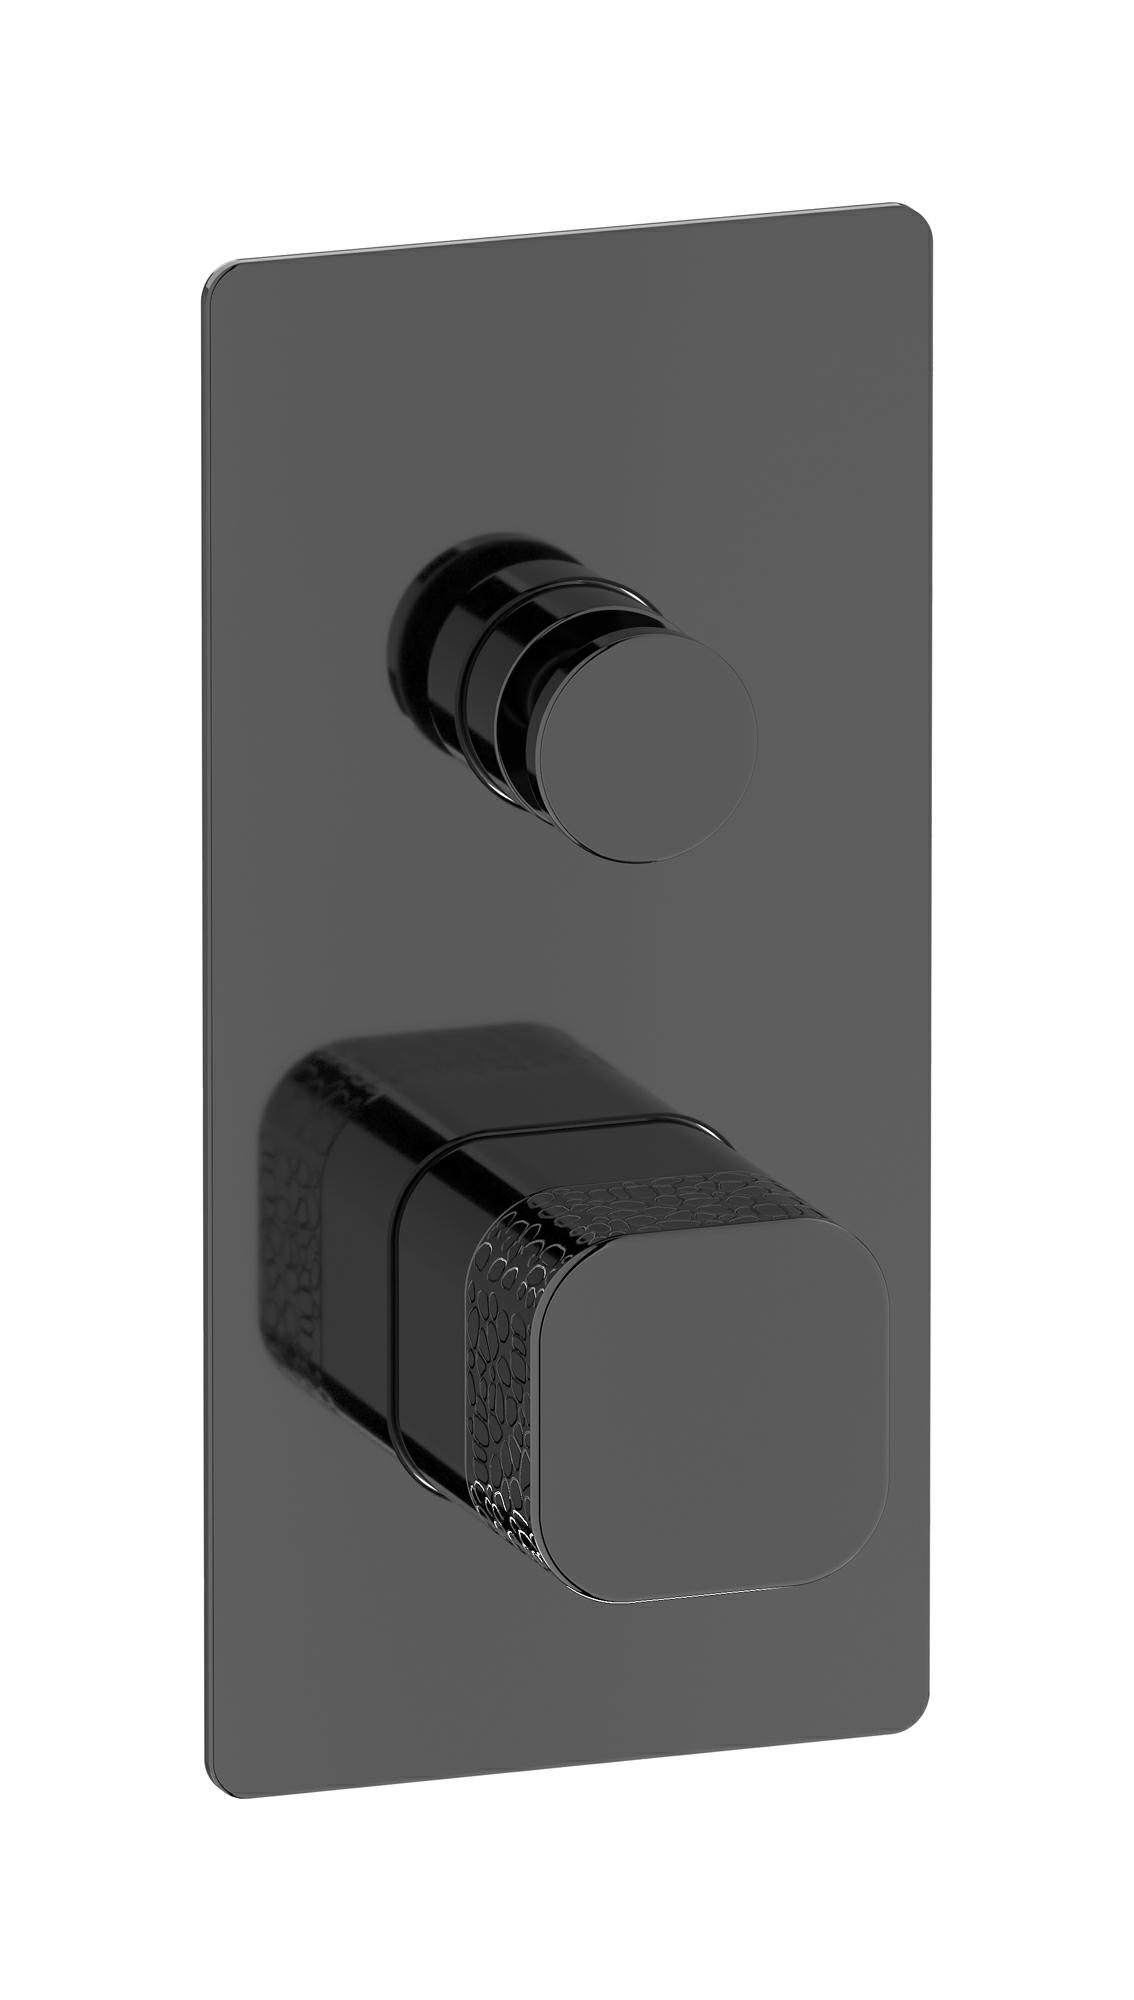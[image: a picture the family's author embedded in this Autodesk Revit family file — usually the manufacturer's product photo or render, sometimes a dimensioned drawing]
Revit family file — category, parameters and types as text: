
# Revit family: EO310_2
name_source: partatom
category: Apparecchi idraulici
units: mm (PartAtom-declared; Revit-internal decimal feet)

## family parameters
Basato su piano di lavoro = No
Condiviso = No
Mantieni orientamento annotazione = No
Numero OmniClass = 23.45.55.17
Punto di calcolo locali = No
Quota connettore circolare = Usa diametro
Sempre verticale = Sì
Taglio con vuoti quando caricato = No
Tipo di parte = Normale
Titolo OmniClass = Mixing Faucets

## types (12) — shared parameters
Cold water inlet = -10 mm  [stored -0.0328084 ft]
Commenti sul tipo = Shower mixer
Connessione CW = No
Connessione HW = No
Connessione di scarico = No
Connessione di ventilazione = No
Descrizione = Two ways shower mixer
Hot water inlet = -10 mm  [stored -0.0328084 ft]
Produttore = IB Rubinetterie S.p.A.
URL = https://www.weareib.it
zero-valued in all types: Prospetto di default

## per-type parameters (varying)
| type | Finishes surface | Immagine tipo | Modello |
| Chrome | IB_Chrome | EO310CC_2.jpg | EO310CC_2 |
| Brushed nickel | IB_Brushed nickel | EO310SS_2.jpg | EO310SS_2 |
| Natural brass | IB_Brass | EO310ON_2.jpg | EO310ON_2 |
| Matt black | IB_matt black | EO310NP_2.jpg | EO310NP_2 |
| Black chrome | IB_Black chrome | EO310CF_2.jpg | EO310CF_2 |
| Brushed black chrome | IB_Brushed black chrome | EO310CS_2.jpg | EO310CS_2 |
| Pale gold | IB_Pale gold | EO310II_2.jpg | EO310II_2 |
| Brushed pale gold | IB_brushed pale gold | EO310IS_2.jpg | EO310IS_2 |
| Rose gold | IB_Rose gold | EO310RS_2.jpg | EO310RS_2 |
| Brushed rose gold | IB_Brushed rose gold | EO310SR_2.jpg | EO310SR_2 |
| Gold | IB_gold | EO310OO_2.jpg | EO310OO_2 |
| Brushed gold | IB_brushed gold | EO310OS_2.jpg | EO310OS_2 |

note: [stored X ft] marks values corroborated as IEEE doubles in the binary element streams (Revit-internal decimal feet)
